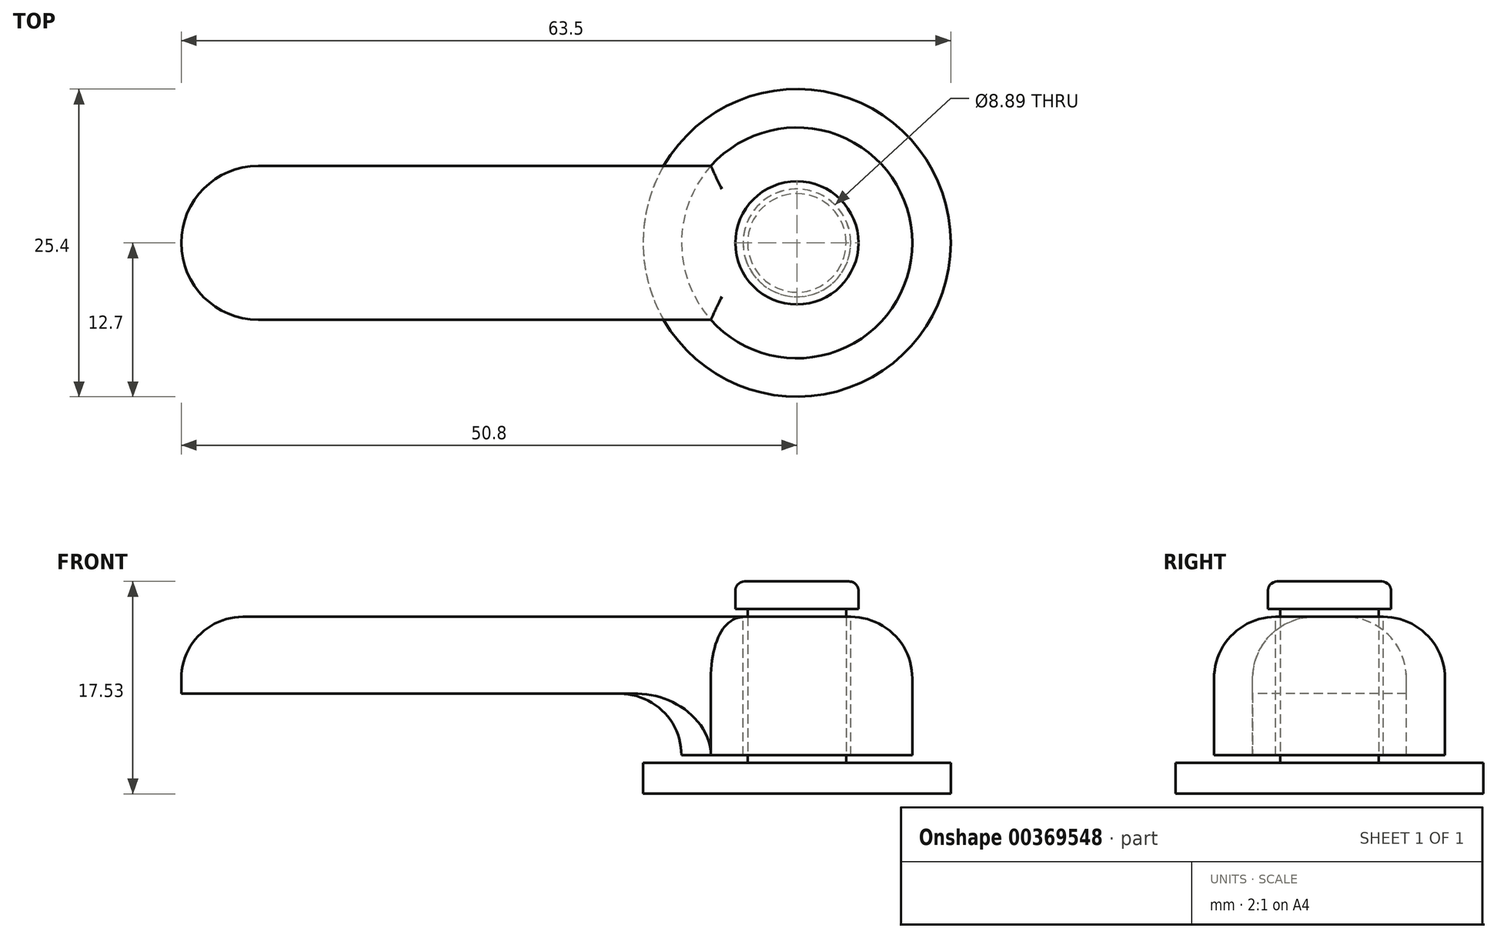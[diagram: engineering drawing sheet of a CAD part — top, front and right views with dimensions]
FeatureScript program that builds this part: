
annotation { "Feature Type Name" : "Feature", "Feature Type Description" : "" }
export const myFeature = defineFeature(function(context is Context, id is Id, definition is map)
    precondition{}
    {
        {
            var Q0;
            Q0=qCreatedBy(makeId("Top.planeOp"),FACE);
            var sketch = newSketch(context, id + "F0", { "sketchPlane" : qUnion([Q0])});
            skCircle(sketch, "E0", {"center": v(0, 0) * mm, "radius": 9.53 * mm});
            skSolve(sketch);
        }
        {
            var Q0;
            Q0 = qSketchRegion(id + "F0", true);
            extrude(context, id + "F1", {"entities" : qUnion([Q0]), "depth" : 11.43 * mm});
        }
        {
            var Q0;
            Q0=makeQuery(id+"F1.opExtrude","CAP_FACE",FACE,{"disambiguationData":[OSD([sQuery(id+"F0.wireOp",EDGE,"E0")])],"isStart":false});
            var sketch = newSketch(context, id + "F2", { "sketchPlane" : qUnion([Q0])});
            skLineSegment(sketch, "E1", {"start": v(-7.1, 6.35) * mm, "end": v(-44.45, 6.35) * mm});
            skLineSegment(sketch, "E2", {"start": v(-50.8, 0) * mm, "end": v(-50.8, 0) * mm});
            skLineSegment(sketch, "E3", {"start": v(-44.45, -6.35) * mm, "end": v(-7.1, -6.35) * mm});
            skPoint(sketch, "E4.visualSharp", {"position": v(-50.8, 6.35) * mm});
            skArc(sketch, "E4.filletArc", {"start": v(-44.45, 6.35) * mm, "mid": v(-48.94, 4.5) * mm, "end": v(-50.8, 0) * mm});
            skPoint(sketch, "E5.visualSharp", {"position": v(-50.8, -6.35) * mm});
            skArc(sketch, "E5.filletArc", {"start": v(-50.8, 0) * mm, "mid": v(-48.94, -4.5) * mm, "end": v(-44.45, -6.35) * mm});
            skLineSegment(sketch, "E6", {"start": v(-7.1, 6.35) * mm, "end": v(-7.1, -6.35) * mm});
            skSolve(sketch);
        }
        {
            var Q0;
            Q0 = qSketchRegion(id + "F2", true);
            extrude(context, id + "F3", {"entities" : qUnion([Q0]), "operationType" : NewBodyOperationType.ADD, "oppositeDirection" : true, "depth" : 6.35 * mm});
        }
        {
            var Q0;
            Q0=makeQuery(id+"F3.boolean.opBoolean","MERGE",FACE,{"derivedFrom":[makeQuery(id+"F1.opExtrude","CAP_FACE",FACE,{"disambiguationData":[OSD([sQuery(id+"F0.wireOp",EDGE,"E0")])],"isStart":false}),makeQuery(id+"F3.opExtrude","CAP_FACE",FACE,{"disambiguationData":[OSD([sQuery(id+"F2.wireOp",EDGE,"E1"),sQuery(id+"F2.wireOp",EDGE,"E3"),sQuery(id+"F2.wireOp",EDGE,"E4.filletArc"),sQuery(id+"F2.wireOp",EDGE,"E5.filletArc"),sQuery(id+"F2.wireOp",EDGE,"E6")])],"isStart":true})]});
            var Q1;
            Q1=makeQuery(id+"F3.boolean.opBoolean","INTERSECT",EDGE,{"derivedFrom":[makeQuery(id+"F1.opExtrude","SWEPT_FACE",FACE,{"disambiguationData":[OSD([sQuery(id+"F0.wireOp",EDGE,"E0")])]}),makeQuery(id+"F3.opExtrude","CAP_FACE",FACE,{"disambiguationData":[OSD([sQuery(id+"F2.wireOp",EDGE,"E1"),sQuery(id+"F2.wireOp",EDGE,"E3"),sQuery(id+"F2.wireOp",EDGE,"E4.filletArc"),sQuery(id+"F2.wireOp",EDGE,"E5.filletArc"),sQuery(id+"F2.wireOp",EDGE,"E6")])],"isStart":false})]});
            fillet(context, id + "F4", {"entities" : qUnion([Q0, Q1]), "radius" : 5.08 * mm, "tangentPropagation" : true, "allowEdgeOverflow" : false});
        }
        {
            var Q0;
            Q0=makeQuery(id+"F3.boolean.opBoolean","MERGE",FACE,{"derivedFrom":[makeQuery(id+"F1.opExtrude","CAP_FACE",FACE,{"disambiguationData":[OSD([sQuery(id+"F0.wireOp",EDGE,"E0")])],"isStart":false}),makeQuery(id+"F3.opExtrude","CAP_FACE",FACE,{"disambiguationData":[OSD([sQuery(id+"F2.wireOp",EDGE,"E1"),sQuery(id+"F2.wireOp",EDGE,"E3"),sQuery(id+"F2.wireOp",EDGE,"E4.filletArc"),sQuery(id+"F2.wireOp",EDGE,"E5.filletArc"),sQuery(id+"F2.wireOp",EDGE,"E6")])],"isStart":true})]});
            var sketch = newSketch(context, id + "F5", { "sketchPlane" : qUnion([Q0])});
            skEllipse(sketch, "E7", {"center": v(0, 0) * mm, "majorRadius": 4.45 * mm, "minorRadius": 4.45 * mm, "majorAxis": v(1, 0)});
            skSolve(sketch);
        }
        {
            var Q0;
            Q0 = qSketchRegion(id + "F5", true);
            extrude(context, id + "F6", {"entities" : qUnion([Q0]), "operationType" : NewBodyOperationType.REMOVE, "endBound" : BoundingType.THROUGH_ALL, "oppositeDirection" : true, "depth" : 25.4 * mm});
        }
        {
            var Q0;
            Q0=qCreatedBy(makeId("Top.planeOp"),FACE);
            var sketch = newSketch(context, id + "F7", { "sketchPlane" : qUnion([Q0])});
            skCircle(sketch, "E8", {"center": v(0, 0) * mm, "radius": 12.7 * mm});
            skSolve(sketch);
        }
        {
            var Q0;
            Q0 = qSketchRegion(id + "F7", true);
            extrude(context, id + "F8", {"entities" : qUnion([Q0]), "oppositeDirection" : true, "depth" : 3.17 * mm, "hasSecondDirection" : true, "secondDirectionOppositeDirection" : false, "secondDirectionDepth" : -0.64 * mm});
        }
        {
            var Q0;
            Q0=makeQuery(id+"F8.opExtrude","CAP_FACE",FACE,{"disambiguationData":[OSD([sQuery(id+"F7.wireOp",EDGE,"E8")])],"isStart":true});
            var sketch = newSketch(context, id + "F9", { "sketchPlane" : qUnion([Q0])});
            skArc(sketch, "E9", {"start": v(0.81, 3.98) * mm, "mid": v(-3.98, 0.81) * mm, "end": v(-0.81, -3.98) * mm});
            skArc(sketch, "E10.trimOffspring", {"start": v(-0.81, -3.98) * mm, "mid": v(3.98, -0.81) * mm, "end": v(0.81, 3.98) * mm});
            skSolve(sketch);
        }
        {
            var Q0;
            Q0 = qSketchRegion(id + "F9", true);
            extrude(context, id + "F10", {"entities" : qUnion([Q0]), "operationType" : NewBodyOperationType.ADD, "depth" : 15 * mm});
        }
        {
            var Q0;
            Q0=makeQuery(id+"F10.opExtrude","CAP_FACE",FACE,{"disambiguationData":[OSD([sQuery(id+"F9.wireOp",EDGE,"E9"),sQuery(id+"F9.wireOp",EDGE,"BGNBN703-bKHs-mL8K-xon0-tf1VI9Vpiba1")])],"isStart":false});
            var sketch = newSketch(context, id + "F11", { "sketchPlane" : qUnion([Q0])});
            skCircle(sketch, "E11", {"center": v(0, 0) * mm, "radius": 5.08 * mm});
            skSolve(sketch);
        }
        {
            var Q0;
            Q0 = qSketchRegion(id + "F11", true);
            extrude(context, id + "F12", {"entities" : qUnion([Q0]), "operationType" : NewBodyOperationType.ADD, "oppositeDirection" : true, "depth" : 2.3 * mm});
        }
        {
            var Q0;
            Q0=makeQuery(id+"F12.opExtrude","CAP_EDGE",EDGE,{"disambiguationData":[OSD([sQuery(id+"F11.wireOp",EDGE,"E11")])],"isStart":true});
            fillet(context, id + "F13", {"entities" : qUnion([Q0]), "radius" : 0.76 * mm, "tangentPropagation" : true, "allowEdgeOverflow" : false});
        }
    });
